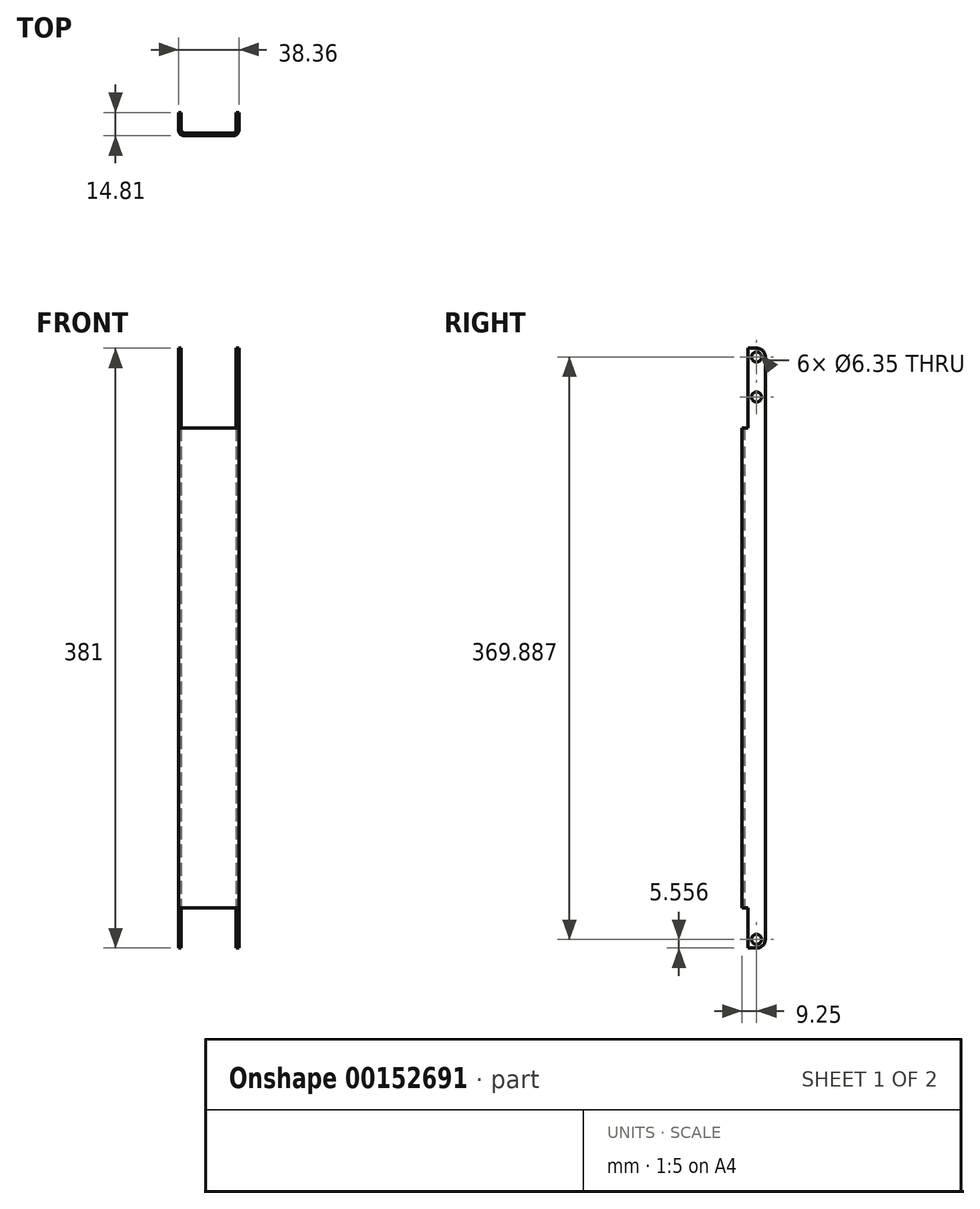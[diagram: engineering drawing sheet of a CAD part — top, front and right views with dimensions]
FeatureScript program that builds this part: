
annotation { "Feature Type Name" : "Feature", "Feature Type Description" : "" }
export const myFeature = defineFeature(function(context is Context, id is Id, definition is map)
    precondition{}
    {
        {
            var Q0;
            Q0=qCreatedBy(makeId("Top.planeOp"),FACE);
            var sketch = newSketch(context, id + "F0", { "sketchPlane" : qUnion([Q0])});
            skLineSegment(sketch, "E0.bottom", {"start": v(0, 0) * mm, "end": v(-34.95, 0) * mm});
            skLineSegment(sketch, "E0.top", {"start": v(1.7, -1.7) * mm, "end": v(-36.65, -1.7) * mm});
            skLineSegment(sketch, "E1.top", {"start": v(-34.95, 13.1) * mm, "end": v(-36.65, 13.1) * mm});
            skLineSegment(sketch, "E1.left", {"start": v(-34.95, 0) * mm, "end": v(-34.95, 13.1) * mm});
            skLineSegment(sketch, "E1.right", {"start": v(-36.65, -1.7) * mm, "end": v(-36.65, 13.1) * mm});
            skLineSegment(sketch, "E2.top", {"start": v(0, 13.1) * mm, "end": v(1.7, 13.1) * mm});
            skLineSegment(sketch, "E2.left", {"start": v(0, 0) * mm, "end": v(0, 13.1) * mm});
            skLineSegment(sketch, "E2.right", {"start": v(1.7, -1.7) * mm, "end": v(1.7, 13.1) * mm});
            skLineSegment(sketch, "E3", {"start": v(-17.47, 0) * mm, "end": v(-17.47, -1.7) * mm, "construction": true});
            skSolve(sketch);
        }
        {
            var Q0;
            Q0=qSketchRegion(id+"F0",true);
            extrude(context, id + "F1", {"entities" : qUnion([Q0]), "depth" : 304.8 * mm});
        }
        {
            var Q0;
            Q0=makeQuery(id+"F1.opExtrude","SWEPT_EDGE",EDGE,{"disambiguationData":[OSD([sQuery(id+"F0.wireOp",EDGE,"E0.top"),sQuery(id+"F0.wireOp",EDGE,"E2.right")])]});
            var Q1;
            Q1=makeQuery(id+"F1.opExtrude","SWEPT_EDGE",EDGE,{"disambiguationData":[OSD([sQuery(id+"F0.wireOp",EDGE,"E0.top"),sQuery(id+"F0.wireOp",EDGE,"E1.right")])]});
            var Q2;
            Q2=makeQuery(id+"FqNnmMD7oaRdpTN_1.opExtrude","CAP_EDGE",EDGE,{"disambiguationData":[OSD([sQuery(id+"FY5sMr6MULj5lJw_1.wireOp",EDGE,"W42EfhJi-fDm4-L9BW-folL-irsYfDskuzBk.top")])],"isStart":false});
            fillet(context, id + "F2", {"entities" : qUnion([Q0, Q1, Q2]), "radius" : 3.7 * mm, "tangentPropagation" : true, "allowEdgeOverflow" : false});
        }
        {
            var Q0;
            Q0=makeQuery(id+"F1.opExtrude","SWEPT_EDGE",EDGE,{"disambiguationData":[OSD([sQuery(id+"F0.wireOp",EDGE,"E0.bottom"),sQuery(id+"F0.wireOp",EDGE,"E2.left")])]});
            var Q1;
            Q1=makeQuery(id+"F1.opExtrude","SWEPT_EDGE",EDGE,{"disambiguationData":[OSD([sQuery(id+"F0.wireOp",EDGE,"E0.bottom"),sQuery(id+"F0.wireOp",EDGE,"E1.left")])]});
            fillet(context, id + "F3", {"entities" : qUnion([Q0, Q1]), "radius" : 1.98 * mm, "tangentPropagation" : true, "allowEdgeOverflow" : false});
        }
        {
            var Q0;
            Q0=makeQuery(id+"F1.opExtrude","SWEPT_FACE",FACE,{"disambiguationData":[OSD([sQuery(id+"F0.wireOp",EDGE,"E1.top")])]});
            var sketch = newSketch(context, id + "F4", { "sketchPlane" : qUnion([Q0])});
            skLineSegment(sketch, "E4.bottom", {"start": v(36.65, 0) * mm, "end": v(34.95, 0) * mm});
            skLineSegment(sketch, "E4.top", {"start": v(36.65, -25.4) * mm, "end": v(34.95, -25.4) * mm});
            skLineSegment(sketch, "E4.left", {"start": v(36.65, 0) * mm, "end": v(36.65, -25.4) * mm});
            skLineSegment(sketch, "E4.right", {"start": v(34.95, 0) * mm, "end": v(34.95, -25.4) * mm});
            skLineSegment(sketch, "E5.bottom", {"start": v(0, 0) * mm, "end": v(-1.7, 0) * mm});
            skLineSegment(sketch, "E5.top", {"start": v(0, -25.4) * mm, "end": v(-1.7, -25.4) * mm});
            skLineSegment(sketch, "E5.left", {"start": v(0, 0) * mm, "end": v(0, -25.4) * mm});
            skLineSegment(sketch, "E5.right", {"start": v(-1.7, 0) * mm, "end": v(-1.7, -25.4) * mm});
            skLineSegment(sketch, "E6.bottom", {"start": v(0, 304.8) * mm, "end": v(-1.7, 304.8) * mm});
            skLineSegment(sketch, "E6.top", {"start": v(0, 355.6) * mm, "end": v(-1.7, 355.6) * mm});
            skLineSegment(sketch, "E6.left", {"start": v(0, 304.8) * mm, "end": v(0, 355.6) * mm});
            skLineSegment(sketch, "E6.right", {"start": v(-1.7, 304.8) * mm, "end": v(-1.7, 355.6) * mm});
            skLineSegment(sketch, "E7.bottom", {"start": v(36.65, 304.8) * mm, "end": v(34.95, 304.8) * mm});
            skLineSegment(sketch, "E7.top", {"start": v(36.65, 355.6) * mm, "end": v(34.95, 355.6) * mm});
            skLineSegment(sketch, "E7.left", {"start": v(36.65, 304.8) * mm, "end": v(36.65, 355.6) * mm});
            skLineSegment(sketch, "E7.right", {"start": v(34.95, 304.8) * mm, "end": v(34.95, 355.6) * mm});
            skSolve(sketch);
        }
        {
            var Q0;
            Q0=makeQuery(id+"F1.opExtrude","SWEPT_FACE",FACE,{"disambiguationData":[OSD([sQuery(id+"F0.wireOp",EDGE,"E0.bottom")])]});
            cPlane(context, id + "F5", {"entities" : qUnion([Q0]), "cplaneType" : CPlaneType.OFFSET, "offset" : 1.98 * mm, "width" : 152.4 * mm, "height" : 152.4 * mm});
        }
        {
            var Q0;
            Q0=makeQuery(id+"F4.imprint","IMPRINT",FACE,{"disambiguationData":[TD([[makeQuery(id+"F4.imprint","IMPRINT",EDGE,{"derivedFrom":sQuery(id+"F4.wireOp",EDGE,"E7.bottom")}),1.0]])]});
            var Q1;
            Q1=makeQuery(id+"F4.imprint","IMPRINT",FACE,{"disambiguationData":[TD([[makeQuery(id+"F4.imprint","IMPRINT",EDGE,{"derivedFrom":sQuery(id+"F4.wireOp",EDGE,"E6.bottom")}),-1.0]])]});
            var Q2;
            Q2=makeQuery(id+"F4.imprint","IMPRINT",FACE,{"disambiguationData":[TD([[makeQuery(id+"F4.imprint","IMPRINT",EDGE,{"derivedFrom":sQuery(id+"F4.wireOp",EDGE,"E5.bottom")}),1.0]])]});
            var Q3;
            Q3=makeQuery(id+"F4.imprint","IMPRINT",FACE,{"disambiguationData":[TD([[makeQuery(id+"F4.imprint","IMPRINT",EDGE,{"derivedFrom":sQuery(id+"F4.wireOp",EDGE,"E4.bottom")}),-1.0]])]});
            var Q4;
            Q4=sQuery(id+"F4.wireOp",EDGE,"E4.left");
            var Q5;
            Q5=sQuery(id+"F4.wireOp",EDGE,"E7.left");
            var Q6;
            Q6=qCreatedBy(id+"F5.planeOp",FACE);
            extrude(context, id + "F6", {"entities" : qUnion([Q0, Q1, Q2, Q3]), "operationType" : NewBodyOperationType.ADD, "surfaceEntities" : qUnion([Q4, Q5]), "endBound" : BoundingType.UP_TO_SURFACE, "oppositeDirection" : true, "endBoundEntityFace" : qUnion([Q6]), "depth" : 25.4 * mm});
        }
        {
            var Q0;
            Q0=makeQuery(id+"F6.opExtrude","TWEAK_EDGE",EDGE,{"derivedFrom":[makeQuery(id+"F4.imprint","IMPRINT",EDGE,{"derivedFrom":sQuery(id+"F4.wireOp",EDGE,"E4.top")}),dummyQuery(id+"F5.planeOp",FACE)]});
            var Q1;
            Q1=makeQuery(id+"F6.opExtrude","CAP_EDGE",EDGE,{"disambiguationData":[OSD([sQuery(id+"F4.wireOp",EDGE,"E4.top")])],"isStart":true});
            var Q2;
            Q2=makeQuery(id+"F6.opExtrude","TWEAK_EDGE",EDGE,{"derivedFrom":[makeQuery(id+"F4.imprint","IMPRINT",EDGE,{"derivedFrom":sQuery(id+"F4.wireOp",EDGE,"E5.top")}),dummyQuery(id+"F5.planeOp",FACE)]});
            var Q3;
            Q3=makeQuery(id+"F6.opExtrude","CAP_EDGE",EDGE,{"disambiguationData":[OSD([sQuery(id+"F4.wireOp",EDGE,"E5.top")])],"isStart":true});
            var Q4;
            Q4=makeQuery(id+"F6.opExtrude","TWEAK_EDGE",EDGE,{"derivedFrom":[makeQuery(id+"F4.imprint","IMPRINT",EDGE,{"derivedFrom":sQuery(id+"F4.wireOp",EDGE,"E6.top")}),dummyQuery(id+"F5.planeOp",FACE)]});
            var Q5;
            Q5=makeQuery(id+"F6.opExtrude","CAP_EDGE",EDGE,{"disambiguationData":[OSD([sQuery(id+"F4.wireOp",EDGE,"E6.top")])],"isStart":true});
            var Q6;
            Q6=makeQuery(id+"F6.opExtrude","TWEAK_EDGE",EDGE,{"derivedFrom":[makeQuery(id+"F4.imprint","IMPRINT",EDGE,{"derivedFrom":sQuery(id+"F4.wireOp",EDGE,"E7.top")}),dummyQuery(id+"F5.planeOp",FACE)]});
            var Q7;
            Q7=makeQuery(id+"F6.opExtrude","CAP_EDGE",EDGE,{"disambiguationData":[OSD([sQuery(id+"F4.wireOp",EDGE,"E7.top")])],"isStart":true});
            fillet(context, id + "F7", {"entities" : qUnion([Q0, Q1, Q2, Q3, Q4, Q5, Q6, Q7]), "radius" : 5.56 * mm, "tangentPropagation" : true, "allowEdgeOverflow" : false});
        }
        {
            var Q0;
            Q0=makeQuery(id+"F6.boolean.opBoolean","MERGE",FACE,{"derivedFrom":[makeQuery(id+"F1.opExtrude","SWEPT_FACE",FACE,{"disambiguationData":[OSD([sQuery(id+"F0.wireOp",EDGE,"E2.right")])]}),makeQuery(id+"F6.opExtrude","SWEPT_FACE",FACE,{"disambiguationData":[OSD([sQuery(id+"F4.wireOp",EDGE,"E5.right")])]}),makeQuery(id+"F6.opExtrude","SWEPT_FACE",FACE,{"disambiguationData":[OSD([sQuery(id+"F4.wireOp",EDGE,"E6.right")])]})]});
            var sketch = newSketch(context, id + "F8", { "sketchPlane" : qUnion([Q0])});
            skCircle(sketch, "E8", {"center": v(7.54, -19.84) * mm, "radius": 3.18 * mm});
            skCircle(sketch, "E9", {"center": v(7.54, 350.04) * mm, "radius": 3.18 * mm});
            skLineSegment(sketch, "E10", {"start": v(7.54, 350.04) * mm, "end": v(7.54, 324.64) * mm, "construction": true});
            skCircle(sketch, "E11", {"center": v(7.54, 324.64) * mm, "radius": 3.18 * mm});
            skSolve(sketch);
        }
        {
            var Q0;
            Q0=qSketchRegion(id+"F8",true);
            var Q1;
            Q1=makeQuery(id+"F6.boolean.opBoolean","MERGE",FACE,{"derivedFrom":[makeQuery(id+"F1.opExtrude","SWEPT_FACE",FACE,{"disambiguationData":[OSD([sQuery(id+"F0.wireOp",EDGE,"E1.right")])]}),makeQuery(id+"F6.opExtrude","SWEPT_FACE",FACE,{"disambiguationData":[OSD([sQuery(id+"F4.wireOp",EDGE,"E4.left")])]}),makeQuery(id+"F6.opExtrude","SWEPT_FACE",FACE,{"disambiguationData":[OSD([sQuery(id+"F4.wireOp",EDGE,"E7.left")])]})]});
            extrude(context, id + "F9", {"entities" : qUnion([Q0]), "operationType" : NewBodyOperationType.REMOVE, "endBound" : BoundingType.UP_TO_SURFACE, "oppositeDirection" : true, "endBoundEntityFace" : qUnion([Q1]), "depth" : 25.4 * mm});
        }
    });
